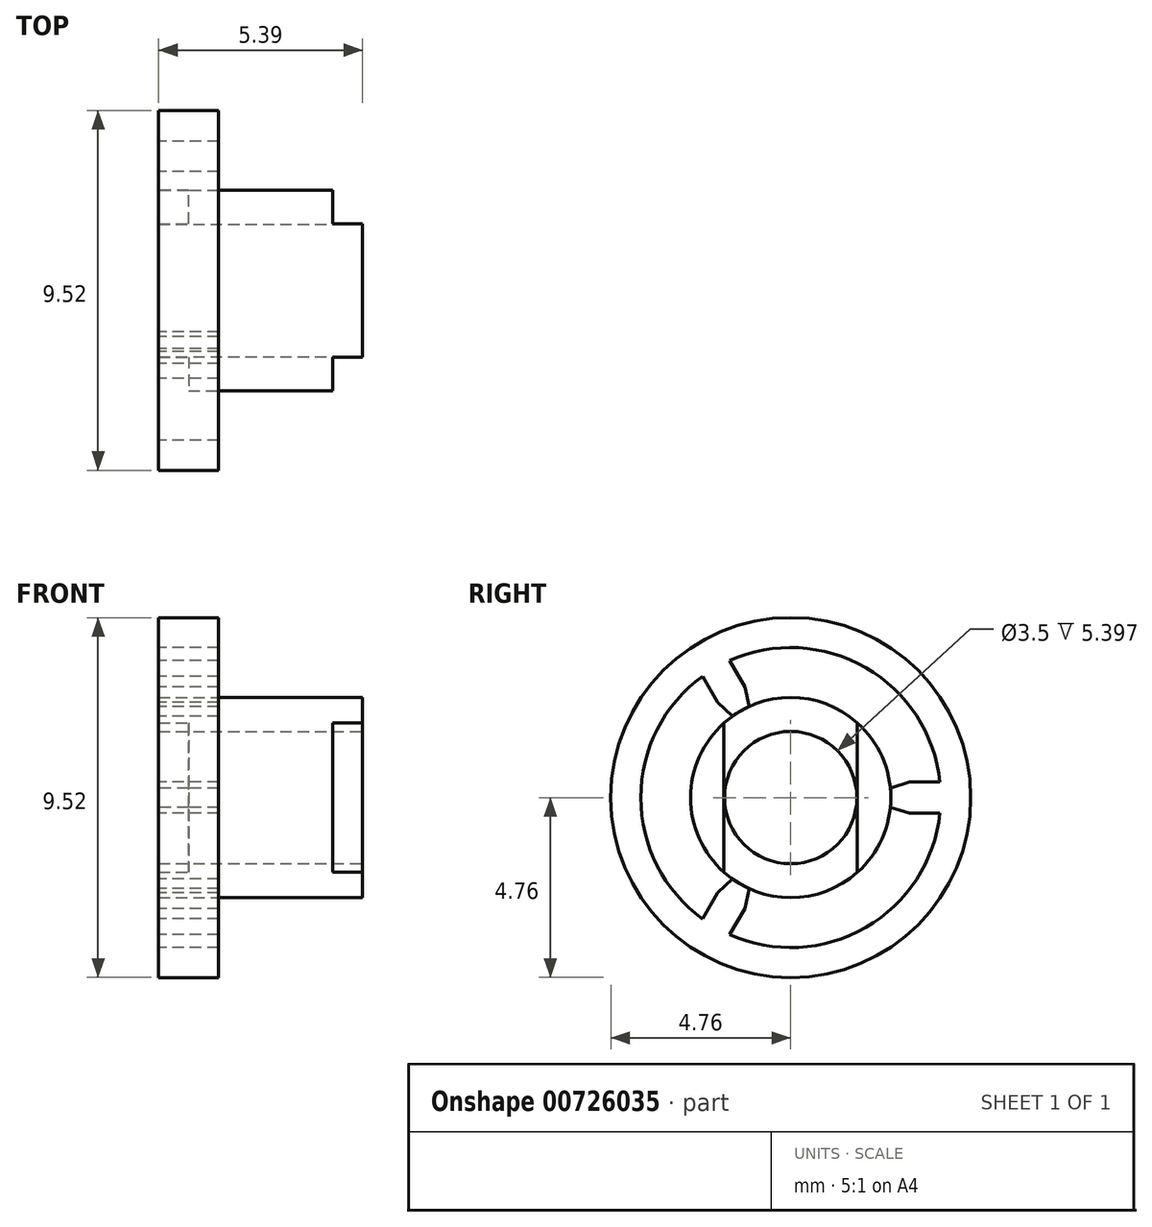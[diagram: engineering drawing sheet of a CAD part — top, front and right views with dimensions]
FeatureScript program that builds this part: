
annotation { "Feature Type Name" : "Feature", "Feature Type Description" : "" }
export const myFeature = defineFeature(function(context is Context, id is Id, definition is map)
    precondition{}
    {
        {
            var Q0;
            Q0=qCreatedBy(makeId("Right.planeOp"),FACE);
            var sketch = newSketch(context, id + "F0", { "sketchPlane" : qUnion([Q0])});
            skCircle(sketch, "E0", {"center": v(0, 0) * mm, "radius": 2.65 * mm});
            skLineSegment(sketch, "E1.bottom", {"start": v(-1.77, 1.98) * mm, "end": v(1.77, 1.98) * mm});
            skLineSegment(sketch, "E1.top", {"start": v(-1.77, -1.98) * mm, "end": v(1.77, -1.98) * mm});
            skLineSegment(sketch, "E1.left", {"start": v(-1.77, 1.98) * mm, "end": v(-1.77, -1.98) * mm});
            skLineSegment(sketch, "E1.right", {"start": v(1.77, 1.98) * mm, "end": v(1.77, -1.98) * mm});
            skCircle(sketch, "E2", {"center": v(0, 0) * mm, "radius": 4.76 * mm});
            skCircle(sketch, "E3", {"center": v(0, 0) * mm, "radius": 3.97 * mm});
            skLineSegment(sketch, "E4", {"start": v(0, 0) * mm, "end": v(4.76, 0) * mm, "construction": true});
            skCircle(sketch, "E5", {"center": v(0, 0) * mm, "radius": 3.18 * mm, "construction": true});
            skLineSegment(sketch, "E6", {"start": v(3.95, 0.41) * mm, "end": v(3.15, 0.41) * mm});
            skLineSegment(sketch, "E7", {"start": v(3.15, 0.41) * mm, "end": v(2.64, 0.25) * mm});
            skLineSegment(sketch, "E8.MirrorCS", {"start": v(3.15, -0.41) * mm, "end": v(2.64, -0.25) * mm});
            skLineSegment(sketch, "E9.MirrorCS", {"start": v(3.95, -0.41) * mm, "end": v(3.15, -0.41) * mm});
            skLineSegment(sketch, "E10.1.0", {"start": v(-2.33, 3.21) * mm, "end": v(-1.93, 2.52) * mm});
            skLineSegment(sketch, "E10.1.1", {"start": v(-1.93, 2.52) * mm, "end": v(-1.54, 2.16) * mm});
            skLineSegment(sketch, "E10.1.2", {"start": v(-1.22, 2.93) * mm, "end": v(-1.1, 2.41) * mm});
            skLineSegment(sketch, "E10.1.3", {"start": v(-1.62, 3.62) * mm, "end": v(-1.22, 2.93) * mm});
            skLineSegment(sketch, "E10.2.0", {"start": v(-1.62, -3.62) * mm, "end": v(-1.22, -2.93) * mm});
            skLineSegment(sketch, "E10.2.1", {"start": v(-1.22, -2.93) * mm, "end": v(-1.1, -2.41) * mm});
            skLineSegment(sketch, "E10.2.2", {"start": v(-1.93, -2.52) * mm, "end": v(-1.54, -2.16) * mm});
            skLineSegment(sketch, "E10.2.3", {"start": v(-2.33, -3.21) * mm, "end": v(-1.93, -2.52) * mm});
            skSolve(sketch);
        }
        {
            var Q0;
            Q0=makeQuery(id+"F0.imprint","IMPRINT",FACE,{"disambiguationData":[TD([[makeQuery(id+"F0.imprint","IMPRINT",EDGE,{"derivedFrom":sQuery(id+"F0.wireOp",EDGE,"E1.bottom")}),-1.0]])]});
            var Q1;
            {var subQ0=sQuery(id+"F0.wireOp",EDGE,"E1.bottom");Q1=makeQuery(id+"F0.imprint","IMPRINT",FACE,{"disambiguationData":[TD([[makeQuery(id+"F0.imprint","IMPRINT",EDGE,{"derivedFrom":subQ0}),1.0]])]});}
            var Q2;
            {var subQ0=sQuery(id+"F0.wireOp",EDGE,"E1.top");Q2=makeQuery(id+"F0.imprint","IMPRINT",FACE,{"disambiguationData":[TD([[makeQuery(id+"F0.imprint","IMPRINT",EDGE,{"derivedFrom":subQ0}),-1.0]])]});}
            extrude(context, id + "F1", {"entities" : qUnion([Q0, Q1, Q2]), "oppositeDirection" : true, "depth" : 0.8 * mm, "offsetDistance" : 25.4 * mm});
        }
        {
            var Q0;
            {var subQ0=sQuery(id+"F0.wireOp",EDGE,"E1.bottom");Q0=makeQuery(id+"F0.imprint","IMPRINT",FACE,{"disambiguationData":[TD([[makeQuery(id+"F0.imprint","IMPRINT",EDGE,{"derivedFrom":subQ0}),1.0]])]});}
            var Q1;
            {var subQ0=sQuery(id+"F0.wireOp",EDGE,"E1.right");Q1=makeQuery(id+"F0.imprint","IMPRINT",FACE,{"disambiguationData":[TD([[makeQuery(id+"F0.imprint","IMPRINT",EDGE,{"derivedFrom":subQ0}),1.0]])]});}
            var Q2;
            {var subQ0=sQuery(id+"F0.wireOp",EDGE,"E1.left");Q2=makeQuery(id+"F0.imprint","IMPRINT",FACE,{"disambiguationData":[TD([[makeQuery(id+"F0.imprint","IMPRINT",EDGE,{"derivedFrom":subQ0}),-1.0]])]});}
            var Q3;
            Q3=makeQuery(id+"F0.imprint","IMPRINT",FACE,{"disambiguationData":[TD([[makeQuery(id+"F0.imprint","IMPRINT",EDGE,{"derivedFrom":sQuery(id+"F0.wireOp",EDGE,"E1.bottom")}),-1.0]])]});
            var Q4;
            {var subQ0=sQuery(id+"F0.wireOp",EDGE,"E1.top");Q4=makeQuery(id+"F0.imprint","IMPRINT",FACE,{"disambiguationData":[TD([[makeQuery(id+"F0.imprint","IMPRINT",EDGE,{"derivedFrom":subQ0}),-1.0]])]});}
            extrude(context, id + "F2", {"entities" : qUnion([Q0, Q1, Q2, Q3, Q4]), "operationType" : NewBodyOperationType.ADD, "depth" : 3.8 * mm, "offsetDistance" : 25.4 * mm});
        }
        {
            var Q0;
            Q0=makeQuery(id+"F2.opExtrude","CAP_FACE",FACE,{"disambiguationData":[OSD([sQuery(id+"F0.wireOp",EDGE,"E0")])],"isStart":false});
            var sketch = newSketch(context, id + "F3", { "sketchPlane" : qUnion([Q0])});
            skLineSegment(sketch, "E11.bottom", {"start": v(-1.77, -1.98) * mm, "end": v(1.77, -1.98) * mm});
            skLineSegment(sketch, "E11.top", {"start": v(-1.77, 1.98) * mm, "end": v(1.77, 1.98) * mm});
            skLineSegment(sketch, "E11.left", {"start": v(-1.77, -1.98) * mm, "end": v(-1.77, 1.98) * mm});
            skLineSegment(sketch, "E11.right", {"start": v(1.77, -1.98) * mm, "end": v(1.77, 1.98) * mm});
            skPoint(sketch, "E11.middle", {"position": v(0, 0) * mm});
            skSolve(sketch);
        }
        {
            var Q0;
            Q0=makeQuery(id+"F3.imprint","IMPRINT",FACE,{"disambiguationData":[TD([[makeQuery(id+"F3.imprint","IMPRINT",EDGE,{"derivedFrom":sQuery(id+"F3.wireOp",EDGE,"E11.bottom")}),1.0]])]});
            var Q1;
            {var subQ0=sQuery(id+"F3.wireOp",EDGE,"E11.top");Q1=makeQuery(id+"F3.imprint","IMPRINT",FACE,{"disambiguationData":[TD([[makeQuery(id+"F3.imprint","IMPRINT",EDGE,{"derivedFrom":subQ0}),1.0]])]});}
            var Q2;
            {var subQ0=sQuery(id+"F3.wireOp",EDGE,"E11.bottom");Q2=makeQuery(id+"F3.imprint","IMPRINT",FACE,{"disambiguationData":[TD([[makeQuery(id+"F3.imprint","IMPRINT",EDGE,{"derivedFrom":subQ0}),-1.0]])]});}
            extrude(context, id + "F4", {"entities" : qUnion([Q0, Q1, Q2]), "operationType" : NewBodyOperationType.ADD, "depth" : 0.8 * mm, "offsetDistance" : 25.4 * mm});
        }
        {
            var Q0;
            Q0=makeQuery(id+"F4.opExtrude","CAP_FACE",FACE,{"disambiguationData":[OSD([sQuery(id+"F3.wireOp",EDGE,"E11.bottom"),sQuery(id+"F3.wireOp",EDGE,"E11.top"),sQuery(id+"F3.wireOp",EDGE,"E11.left"),sQuery(id+"F3.wireOp",EDGE,"E11.right")])],"isStart":false});
            var sketch = newSketch(context, id + "F5", { "sketchPlane" : qUnion([Q0])});
            skCircle(sketch, "E12", {"center": v(0, 0) * mm, "radius": 1.75 * mm});
            skSolve(sketch);
        }
        {
            var Q0;
            Q0 = qSketchRegion(id + "F5", true);
            extrude(context, id + "F6", {"entities" : qUnion([Q0]), "operationType" : NewBodyOperationType.REMOVE, "endBound" : BoundingType.THROUGH_ALL, "oppositeDirection" : true, "depth" : 25.4 * mm, "offsetDistance" : 25.4 * mm});
        }
        {
            var Q0;
            Q0=makeQuery(id+"F0.imprint","IMPRINT",FACE,{"disambiguationData":[TD([[makeQuery(id+"F0.imprint","IMPRINT",EDGE,{"derivedFrom":sQuery(id+"F0.wireOp",EDGE,"E2")}),1.0]])]});
            var Q1;
            {var subQ1=sQuery(id+"F0.wireOp",EDGE,"E6");Q1=makeQuery(id+"F0.imprint","IMPRINT",FACE,{"disambiguationData":[TD([[makeQuery(id+"F0.imprint","IMPRINT",EDGE,{"derivedFrom":subQ1}),1.0]])]});}
            var Q2;
            {var subQ0=sQuery(id+"F0.wireOp",EDGE,"E10.1.0");Q2=makeQuery(id+"F0.imprint","IMPRINT",FACE,{"disambiguationData":[TD([[makeQuery(id+"F0.imprint","IMPRINT",EDGE,{"derivedFrom":subQ0}),1.0]])]});}
            var Q3;
            {var subQ0=sQuery(id+"F0.wireOp",EDGE,"E10.2.0");Q3=makeQuery(id+"F0.imprint","IMPRINT",FACE,{"disambiguationData":[TD([[makeQuery(id+"F0.imprint","IMPRINT",EDGE,{"derivedFrom":subQ0}),1.0]])]});}
            extrude(context, id + "F7", {"entities" : qUnion([Q0, Q1, Q2, Q3]), "operationType" : NewBodyOperationType.ADD, "depth" : 1.59 * mm, "offsetDistance" : 25.4 * mm, "symmetric" : true});
        }
    });
